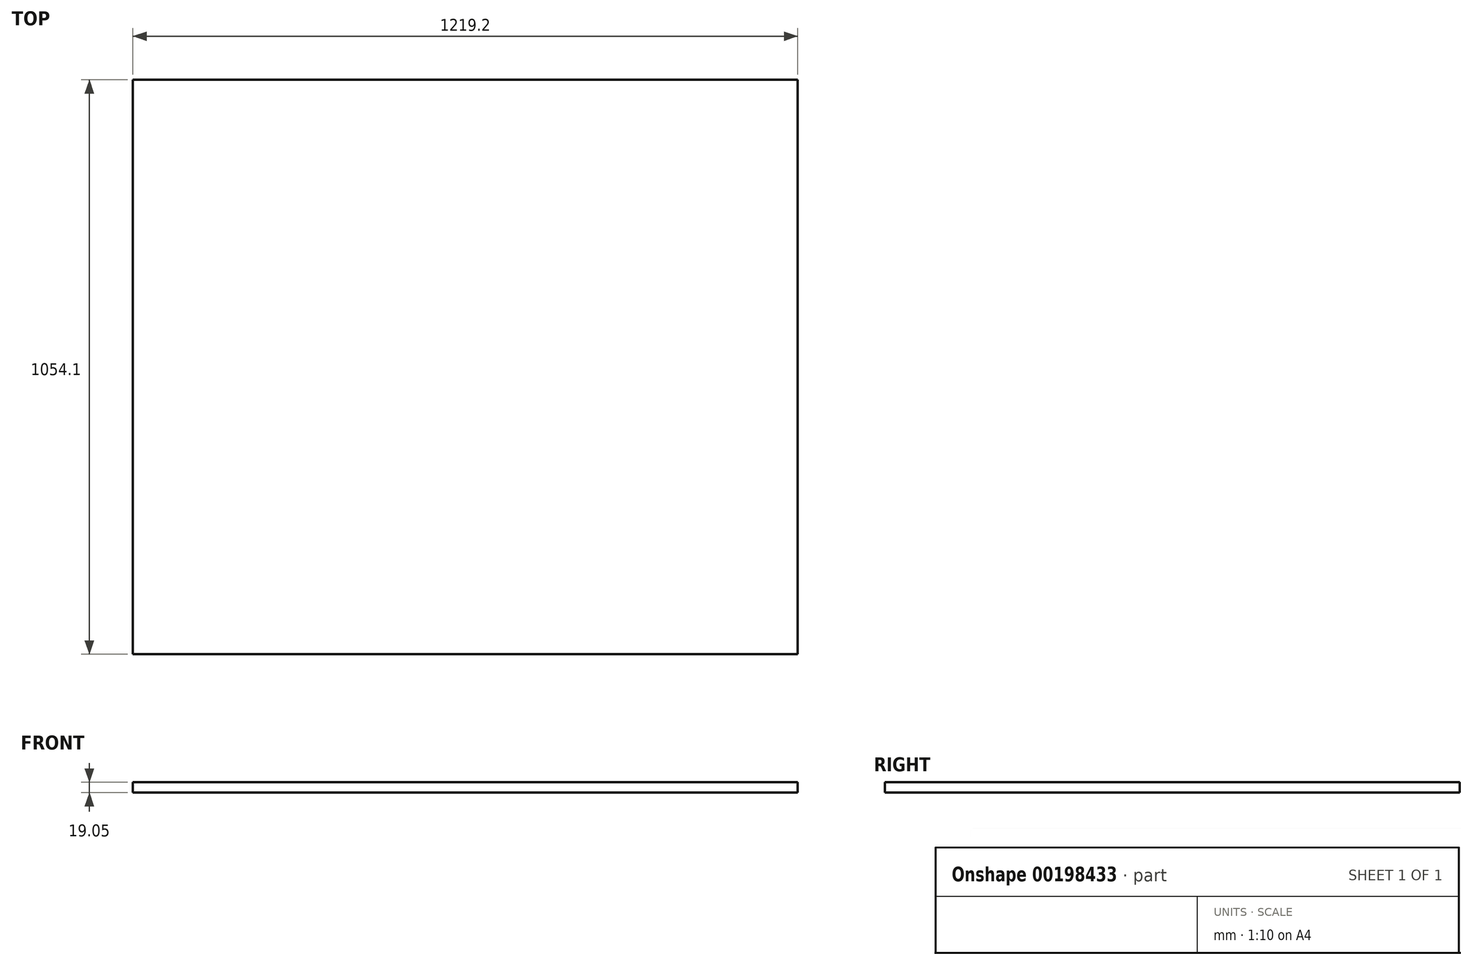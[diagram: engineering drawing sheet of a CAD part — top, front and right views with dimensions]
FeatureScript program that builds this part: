
annotation { "Feature Type Name" : "Feature", "Feature Type Description" : "" }
export const myFeature = defineFeature(function(context is Context, id is Id, definition is map)
    precondition{}
    {
        {
            var Q0;
            Q0=qCreatedBy(makeId("Top.planeOp"),FACE);
            var sketch = newSketch(context, id + "F0", { "sketchPlane" : qUnion([Q0])});
            skLineSegment(sketch, "E0.bottom", {"start": v(0, 0) * mm, "end": v(1219.2, 0) * mm});
            skLineSegment(sketch, "E0.top", {"start": v(0, 1054.1) * mm, "end": v(1219.2, 1054.1) * mm});
            skLineSegment(sketch, "E0.left", {"start": v(0, 0) * mm, "end": v(0, 1054.1) * mm});
            skLineSegment(sketch, "E0.right", {"start": v(1219.2, 0) * mm, "end": v(1219.2, 1054.1) * mm});
            skSolve(sketch);
        }
        {
            var Q0;
            Q0 = qSketchRegion(id + "F0", true);
            extrude(context, id + "F1", {"entities" : qUnion([Q0]), "depth" : 19.05 * mm});
        }
    });
